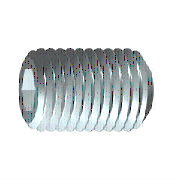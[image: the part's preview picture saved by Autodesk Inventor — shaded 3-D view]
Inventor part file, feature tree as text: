
AUTODESK INVENTOR PART (.ipt)
format: ipt  version: 2019 (Build 230136000, 136)  size: 178,688 bytes
history: native  units: mm (DEFAULTED — no unit token found)
features: sketch x2, extrude x1, other x1, plane x1
ambient origin geometry x8: Origin, YZ Plane, XZ Plane, XY Plane, X Axis, Y Axis, Z Axis, Center Point
bodies: Solid1 (feature_tree), Body (feature_tree)
feature tree (5):
  extrude  "Slot"  TaperAngle=60.0deg  [1 undecoded]
  other  "Work Axis1"
  plane  "Work Plane1"
  sketch  "Sketch1"  dims[d0=1.2mm d1=60.0deg]
  sketch  "Sketch2"  dims[d2=3.0mm d3=1.732051mm d6=90.0deg d4=4.0mm d5=60.0deg d7=1.4mm d8=1.2mm d9=0.0mm d10=0.8mm d11=60.0deg d12=0.306725mm d13=60.0deg d14=4.0mm d15=0.0mm d16=0.0mm d33=0.8mm d34=0.306725mm d35=0.0mm d37=0.0mm]
note: 1 required parameter value undecoded (feature->parameter linkage not recoverable at this tier; creation-order binding heuristic only, values carry confidence <= 0.55)
